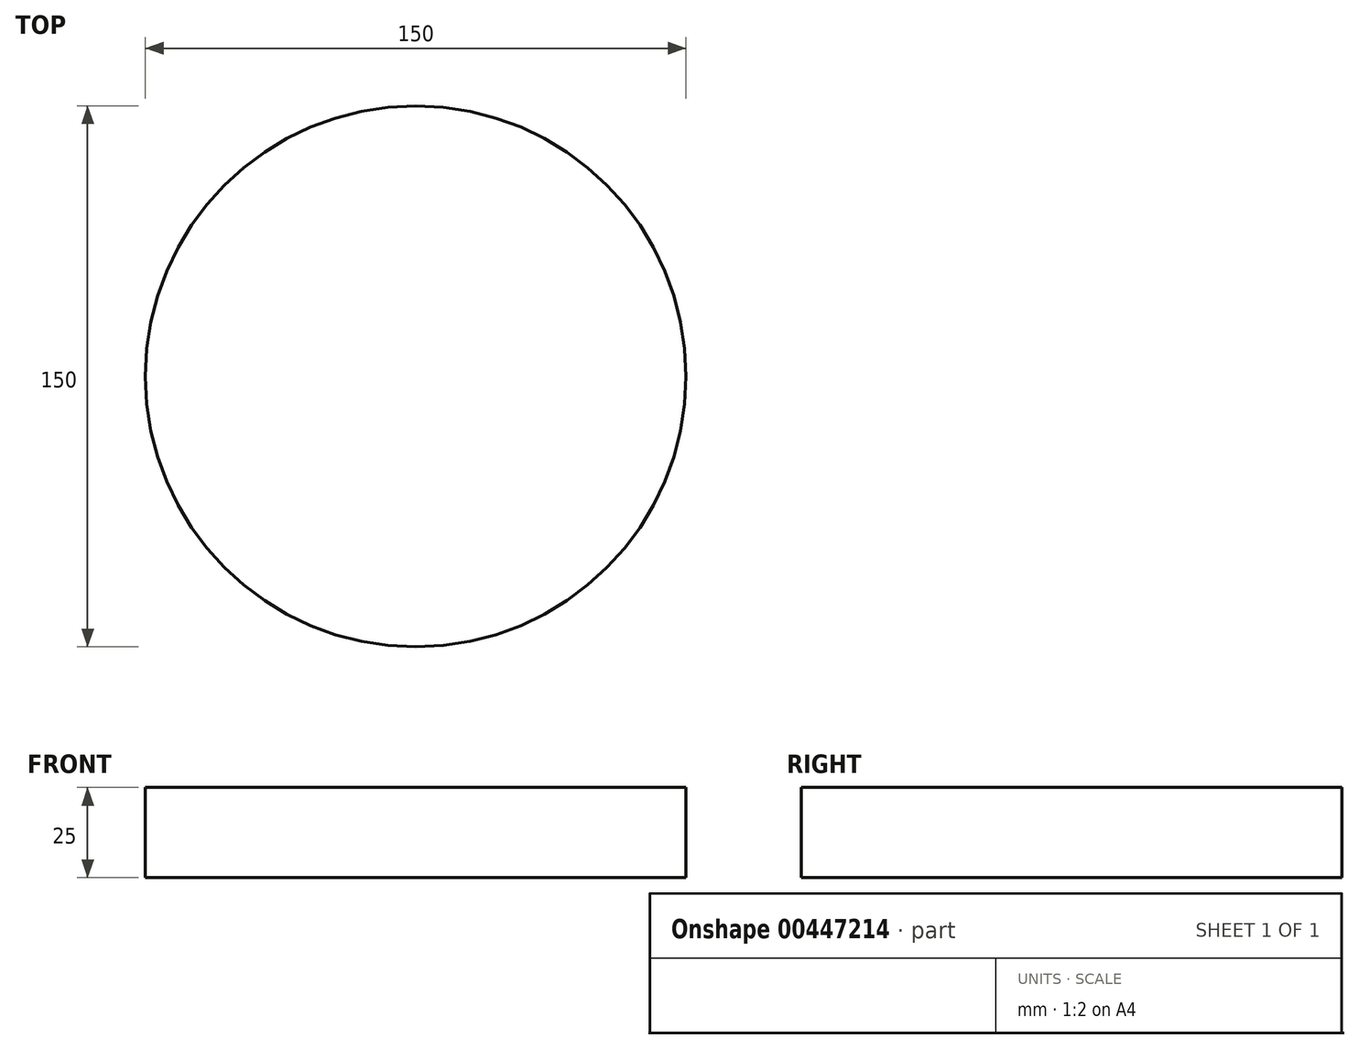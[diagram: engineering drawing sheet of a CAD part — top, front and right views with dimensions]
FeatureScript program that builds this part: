
annotation { "Feature Type Name" : "Feature", "Feature Type Description" : "" }
export const myFeature = defineFeature(function(context is Context, id is Id, definition is map)
    precondition{}
    {
        {
            var Q0;
            Q0=qCreatedBy(makeId("Top.planeOp"),FACE);
            var sketch = newSketch(context, id + "F0", { "sketchPlane" : qUnion([Q0])});
            skCircle(sketch, "E0", {"center": v(0, 0) * mm, "radius": 75 * mm});
            skSolve(sketch);
        }
        {
            var Q0;
            Q0 = qSketchRegion(id + "F0", true);
            extrude(context, id + "F1", {"entities" : qUnion([Q0]), "depth" : 25 * mm});
        }
    });
